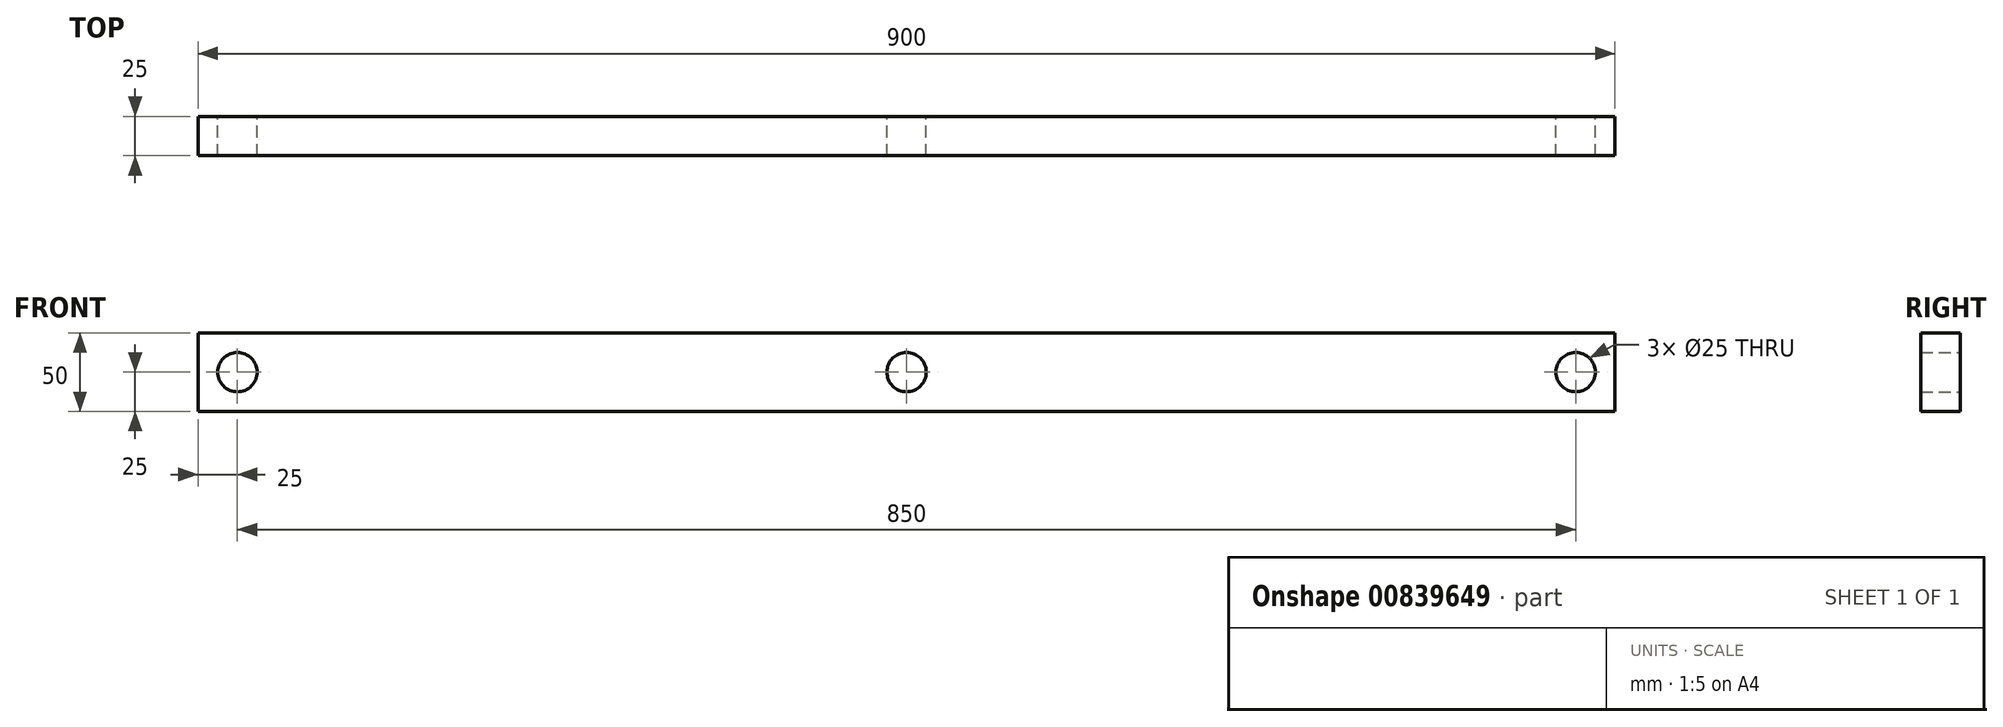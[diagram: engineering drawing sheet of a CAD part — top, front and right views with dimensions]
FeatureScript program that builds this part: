
annotation { "Feature Type Name" : "Feature", "Feature Type Description" : "" }
export const myFeature = defineFeature(function(context is Context, id is Id, definition is map)
    precondition{}
    {
        {
            var Q0;
            Q0=qCreatedBy(makeId("Front.planeOp"),FACE);
            var sketch = newSketch(context, id + "F0", { "sketchPlane" : qUnion([Q0])});
            skLineSegment(sketch, "E0.bottom", {"start": v(0, 0) * mm, "end": v(-900, 0) * mm});
            skLineSegment(sketch, "E0.top", {"start": v(0, -50) * mm, "end": v(-900, -50) * mm});
            skLineSegment(sketch, "E0.left", {"start": v(0, 0) * mm, "end": v(0, -50) * mm});
            skLineSegment(sketch, "E0.right", {"start": v(-900, 0) * mm, "end": v(-900, -50) * mm});
            skLineSegment(sketch, "E1", {"start": v(0, 0) * mm, "end": v(-50, -50) * mm});
            skCircle(sketch, "E2", {"center": v(-25, -25) * mm, "radius": 12.5 * mm});
            skLineSegment(sketch, "E3", {"start": v(-900, 0) * mm, "end": v(-850, -50) * mm});
            skCircle(sketch, "E4", {"center": v(-875, -25) * mm, "radius": 12.5 * mm});
            skLineSegment(sketch, "E5", {"start": v(-875, -25) * mm, "end": v(-25, -25) * mm, "construction": true});
            skCircle(sketch, "E6", {"center": v(-450, -25) * mm, "radius": 12.5 * mm});
            skSolve(sketch);
        }
        {
            var Q0;
            Q0=makeQuery(id+"F0.imprint","IMPRINT",FACE,{"disambiguationData":[TD([[makeQuery(id+"F0.imprint","IMPRINT",EDGE,{"derivedFrom":sQuery(id+"F0.wireOp",EDGE,"E0.bottom")}),1.0]])]});
            var Q1;
            {var subQ5=sQuery(id+"F0.wireOp",EDGE,"E0.left");Q1=makeQuery(id+"F0.imprint","IMPRINT",FACE,{"disambiguationData":[TD([[makeQuery(id+"F0.imprint","IMPRINT",EDGE,{"derivedFrom":subQ5}),-1.0]])]});}
            var Q2;
            {var subQ1=sQuery(id+"F0.wireOp",EDGE,"E0.right");Q2=makeQuery(id+"F0.imprint","IMPRINT",FACE,{"disambiguationData":[TD([[makeQuery(id+"F0.imprint","IMPRINT",EDGE,{"derivedFrom":subQ1}),1.0]])]});}
            extrude(context, id + "F1", {"entities" : qUnion([Q0, Q1, Q2]), "depth" : 25 * mm, "offsetDistance" : 25 * mm});
        }
    });
